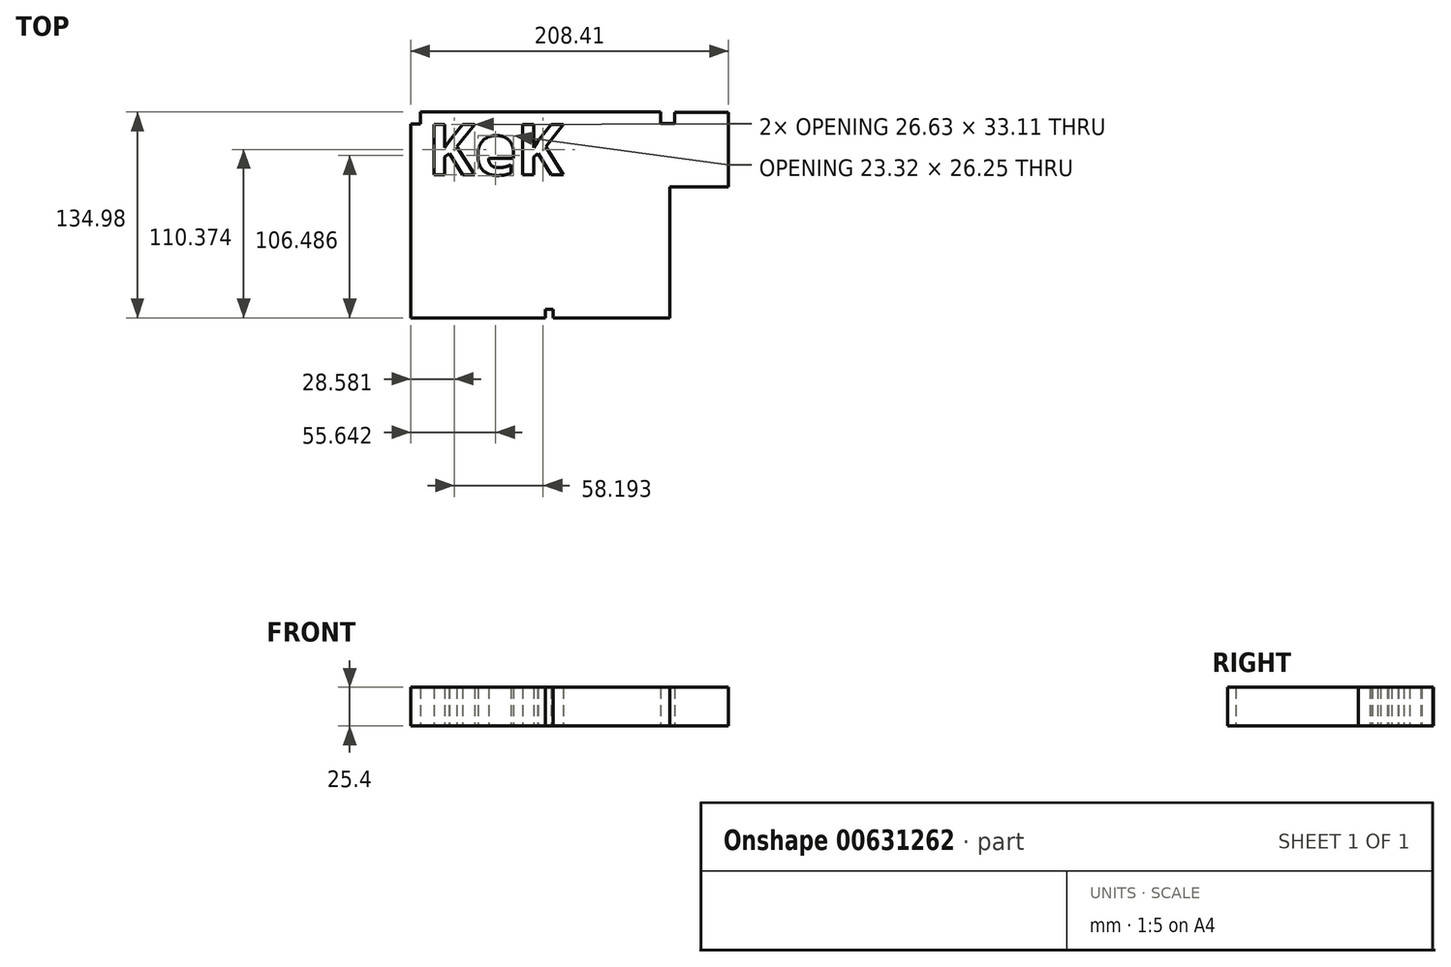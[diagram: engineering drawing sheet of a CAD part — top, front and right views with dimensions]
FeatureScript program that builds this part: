
annotation { "Feature Type Name" : "Feature", "Feature Type Description" : "" }
export const myFeature = defineFeature(function(context is Context, id is Id, definition is map)
    precondition{}
    {
        {
            var Q0;
            Q0=qCreatedBy(makeId("Top.planeOp"),FACE);
            var sketch = newSketch(context, id + "F0", { "sketchPlane" : qUnion([Q0])});
            skLineSegment(sketch, "E0", {"start": v(-111.81, 68.07) * mm, "end": v(-111.81, -59.14) * mm});
            skLineSegment(sketch, "E1", {"start": v(-111.81, 68.07) * mm, "end": v(-105.48, 68.07) * mm});
            skLineSegment(sketch, "E2", {"start": v(-105.48, 68.07) * mm, "end": v(-105.48, 75.84) * mm});
            skLineSegment(sketch, "E3", {"start": v(-105.48, 75.84) * mm, "end": v(52.16, 75.84) * mm});
            skLineSegment(sketch, "E4", {"start": v(52.16, 75.84) * mm, "end": v(52.16, 68.4) * mm});
            skLineSegment(sketch, "E5", {"start": v(52.16, 68.4) * mm, "end": v(61.2, 68.4) * mm});
            skLineSegment(sketch, "E6", {"start": v(61.2, 68.4) * mm, "end": v(61.2, 75.74) * mm});
            skLineSegment(sketch, "E7", {"start": v(61.2, 75.74) * mm, "end": v(96.6, 75.74) * mm});
            skLineSegment(sketch, "E8", {"start": v(96.6, 75.74) * mm, "end": v(96.6, 26.69) * mm});
            skLineSegment(sketch, "E9", {"start": v(96.6, 26.69) * mm, "end": v(57.89, 26.69) * mm});
            skLineSegment(sketch, "E10", {"start": v(57.89, 26.69) * mm, "end": v(57.89, -59.14) * mm});
            skLineSegment(sketch, "E11", {"start": v(57.89, -59.14) * mm, "end": v(-18.4, -59.14) * mm});
            skLineSegment(sketch, "E12", {"start": v(-18.4, -59.14) * mm, "end": v(-18.4, -53.68) * mm});
            skLineSegment(sketch, "E13", {"start": v(-23.68, -53.68) * mm, "end": v(-23.68, -59.14) * mm});
            skLineSegment(sketch, "E14", {"start": v(-23.68, -53.68) * mm, "end": v(-18.4, -53.68) * mm});
            skLineSegment(sketch, "E15", {"start": v(-111.81, -59.14) * mm, "end": v(-23.68, -59.14) * mm});
            skText(sketch, "E16", { "text": "KeK\n", "fontName": "OpenSans-Bold.ttf"});
            const initialGuessF0  = {"E16": [-0.10071, 0.03468, 1, 0, 0.03339]};
            skSetInitialGuess(sketch, initialGuessF0);
            skSolve(sketch);
        }
        {
            var Q0;
            Q0 = qSketchRegion(id + "F0", true);
            extrude(context, id + "F1", {"entities" : qUnion([Q0]), "depth" : 7.62 * mm, "offsetDistance" : 25.4 * mm});
        }
        {
            var Q0;
            Q0 = qSketchRegion(id + "F0", true);
            extrude(context, id + "F2", {"entities" : qUnion([Q0]), "operationType" : NewBodyOperationType.ADD, "depth" : 25.4 * mm, "offsetDistance" : 25.4 * mm});
        }
    });
